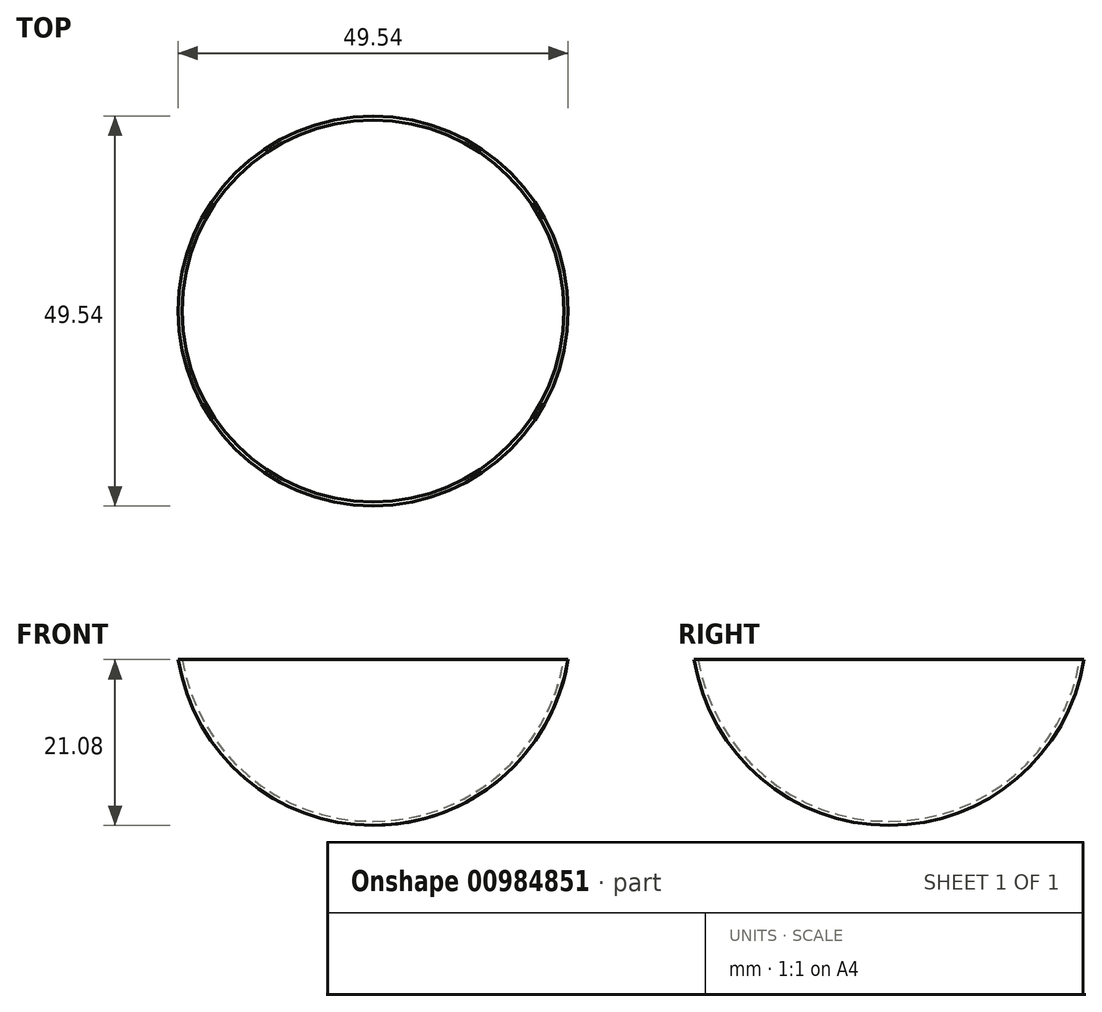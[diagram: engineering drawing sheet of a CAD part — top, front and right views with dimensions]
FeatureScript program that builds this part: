
annotation { "Feature Type Name" : "Feature", "Feature Type Description" : "" }
export const myFeature = defineFeature(function(context is Context, id is Id, definition is map)
    precondition{}
    {
        {
            var Q0;
            Q0=qCreatedBy(makeId("Front.planeOp"),FACE);
            var sketch = newSketch(context, id + "F0", { "sketchPlane" : qUnion([Q0])});
            skLineSegment(sketch, "E0", {"start": v(0, 21.08) * mm, "end": v(0, 0) * mm});
            skLineSegment(sketch, "E1", {"start": v(0, 21.08) * mm, "end": v(24.77, 21.08) * mm});
            skArc(sketch, "E2", {"start": v(0, 0) * mm, "mid": v(16.26, 5.98) * mm, "end": v(24.77, 21.08) * mm});
            skLineSegment(sketch, "E3", {"start": v(-10.61, 0) * mm, "end": v(15.94, 0) * mm, "construction": true});
            skSolve(sketch);
        }
        {
            var Q0;
            Q0 = qSketchRegion(id + "F0", true);
            var Q1;
            Q1=sQuery(id+"F0.wireOp",EDGE,"E0");
            revolve(context, id + "F1", {"surfaceOperationType" : NewSurfaceOperationType.NEW, "entities" : qUnion([Q0]), "axis" : qUnion([Q1]), "revolveType" : RevolveType.FULL});
        }
        {
            var Q0;
            Q0=makeQuery(id+"F1.opRevolve","SWEPT_FACE",FACE,{"disambiguationData":[OSD([sQuery(id+"F0.wireOp",EDGE,"E1")])]});
            var Q1;
            Q1=makeQuery(id+"F1.opRevolve","SWEPT_BODY",BODY,{"disambiguationData":[OSD([sQuery(id+"F0.wireOp",EDGE,"E0"),sQuery(id+"F0.wireOp",EDGE,"E1"),sQuery(id+"F0.wireOp",EDGE,"E2")])]});
            shell(context, id + "F2", {"entities" : qUnion([Q0]), "parts" : qUnion([Q1]), "thickness" : 0.5 * mm});
        }
    });
